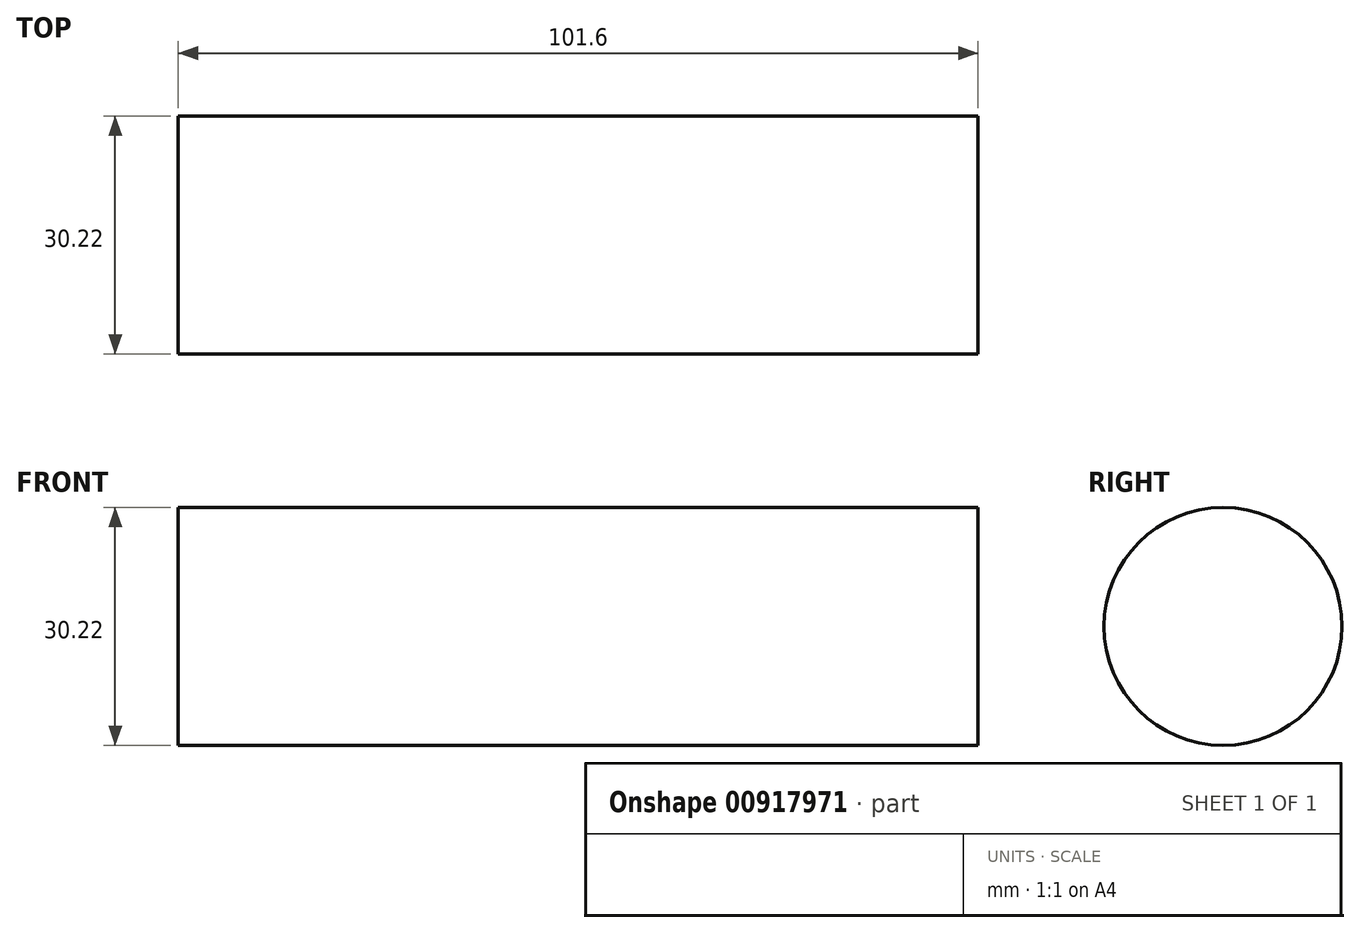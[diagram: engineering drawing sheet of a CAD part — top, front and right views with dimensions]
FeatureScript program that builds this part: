
annotation { "Feature Type Name" : "Feature", "Feature Type Description" : "" }
export const myFeature = defineFeature(function(context is Context, id is Id, definition is map)
    precondition{}
    {
        {
            var Q0;
            Q0=qCreatedBy(makeId("Right.planeOp"),FACE);
            var sketch = newSketch(context, id + "F0", { "sketchPlane" : qUnion([Q0])});
            skCircle(sketch, "E0", {"center": v(0, 0) * mm, "radius": 15.11 * mm});
            skSolve(sketch);
        }
        {
            var Q0;
            Q0=makeQuery(id+"F0.imprint","IMPRINT",FACE,{"disambiguationData":[TD([[makeQuery(id+"F0.imprint","IMPRINT",EDGE,{"derivedFrom":sQuery(id+"F0.wireOp",EDGE,"E0")}),1.0]])]});
            extrude(context, id + "F1", {"entities" : qUnion([Q0]), "depth" : 101.6 * mm, "offsetDistance" : 25.4 * mm});
        }
    });
